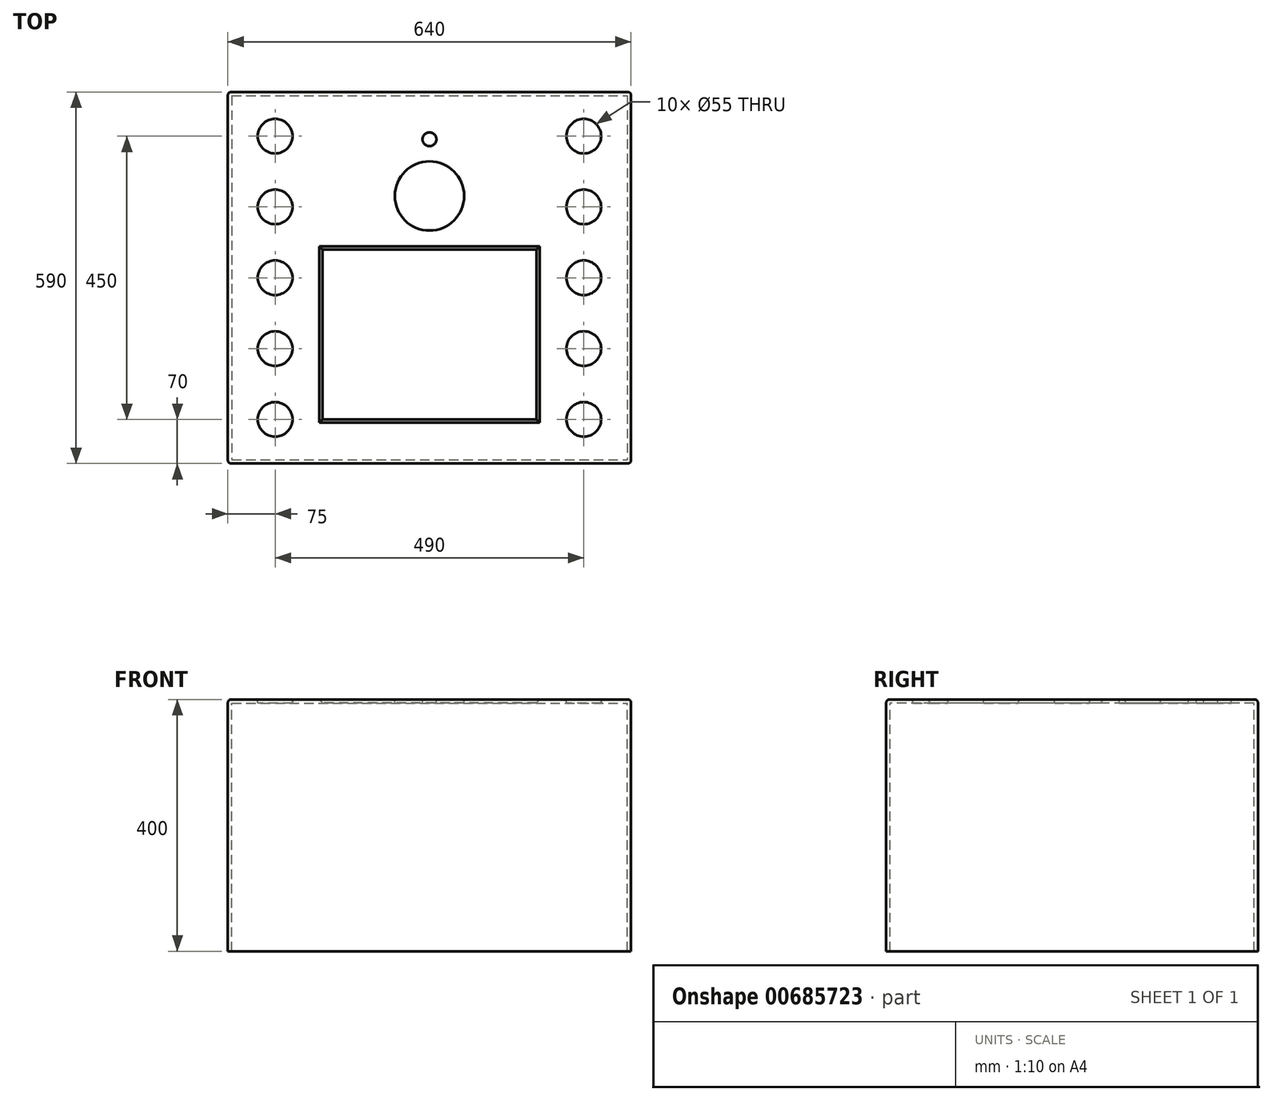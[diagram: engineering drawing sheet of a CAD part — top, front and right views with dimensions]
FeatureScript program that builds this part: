
annotation { "Feature Type Name" : "Feature", "Feature Type Description" : "" }
export const myFeature = defineFeature(function(context is Context, id is Id, definition is map)
    precondition{}
    {
        {
            var Q0;
            Q0=qCreatedBy(makeId("Top.planeOp"),FACE);
            var sketch = newSketch(context, id + "F0", { "sketchPlane" : qUnion([Q0])});
            skLineSegment(sketch, "E0.bottom", {"start": v(320, 295) * mm, "end": v(-320, 295) * mm});
            skLineSegment(sketch, "E0.top", {"start": v(320, -295) * mm, "end": v(-320, -295) * mm});
            skLineSegment(sketch, "E0.left", {"start": v(320, 295) * mm, "end": v(320, -295) * mm});
            skLineSegment(sketch, "E0.right", {"start": v(-320, 295) * mm, "end": v(-320, -295) * mm});
            skPoint(sketch, "E0.middle", {"position": v(0, 0) * mm});
            skLineSegment(sketch, "E1.bottom", {"start": v(170, 45) * mm, "end": v(-170, 45) * mm});
            skLineSegment(sketch, "E1.top", {"start": v(170, -225) * mm, "end": v(-170, -225) * mm});
            skLineSegment(sketch, "E1.left", {"start": v(170, 45) * mm, "end": v(170, -225) * mm});
            skLineSegment(sketch, "E1.right", {"start": v(-170, 45) * mm, "end": v(-170, -225) * mm});
            skPoint(sketch, "E1.middle", {"position": v(0, -90) * mm});
            skCircle(sketch, "E2", {"center": v(0, 130) * mm, "radius": 55 * mm});
            skCircle(sketch, "E3", {"center": v(0, 220) * mm, "radius": 11 * mm});
            skCircle(sketch, "E4", {"center": v(-245, -225) * mm, "radius": 27.5 * mm});
            skCircle(sketch, "E5.0.1.0", {"center": v(-245, -112.5) * mm, "radius": 27.5 * mm});
            skCircle(sketch, "E5.0.2.0", {"center": v(-245, 0) * mm, "radius": 27.5 * mm});
            skCircle(sketch, "E5.0.3.0", {"center": v(-245, 112.5) * mm, "radius": 27.5 * mm});
            skCircle(sketch, "E5.1.0.0", {"center": v(245, -225) * mm, "radius": 27.5 * mm});
            skCircle(sketch, "E5.1.1.0", {"center": v(245, -112.5) * mm, "radius": 27.5 * mm});
            skCircle(sketch, "E5.1.2.0", {"center": v(245, 0) * mm, "radius": 27.5 * mm});
            skCircle(sketch, "E5.1.3.0", {"center": v(245, 112.5) * mm, "radius": 27.5 * mm});
            skLineSegment(sketch, "E5.direction1", {"start": v(-245, -225) * mm, "end": v(245, -225) * mm, "construction": true});
            skLineSegment(sketch, "E5.direction2", {"start": v(-245, -225) * mm, "end": v(-245, -112.5) * mm, "construction": true});
            skLineSegment(sketch, "E6.bottom", {"start": v(-314, 289) * mm, "end": v(314, 289) * mm});
            skLineSegment(sketch, "E6.top", {"start": v(-314, -289) * mm, "end": v(314, -289) * mm});
            skLineSegment(sketch, "E6.left", {"start": v(-314, 289) * mm, "end": v(-314, -289) * mm});
            skLineSegment(sketch, "E6.right", {"start": v(314, 289) * mm, "end": v(314, -289) * mm});
            skCircle(sketch, "E7.0.0.4", {"center": v(-245, 225) * mm, "radius": 27.5 * mm});
            skCircle(sketch, "E7.0.1.4", {"center": v(245, 225) * mm, "radius": 27.5 * mm});
            skSolve(sketch);
        }
        {
            var Q0;
            Q0=makeQuery(id+"F0.imprint","IMPRINT",FACE,{"disambiguationData":[TD([[makeQuery(id+"F0.imprint","IMPRINT",EDGE,{"derivedFrom":sQuery(id+"F0.wireOp",EDGE,"E0.bottom")}),1.0]])]});
            extrude(context, id + "F1", {"entities" : qUnion([Q0]), "oppositeDirection" : true, "depth" : 400 * mm, "offsetDistance" : 25 * mm});
        }
        {
            var Q0;
            Q0=makeQuery(id+"F0.imprint","IMPRINT",FACE,{"disambiguationData":[TD([[makeQuery(id+"F0.imprint","IMPRINT",EDGE,{"derivedFrom":sQuery(id+"F0.wireOp",EDGE,"E1.bottom")}),-1.0]])]});
            extrude(context, id + "F2", {"entities" : qUnion([Q0]), "operationType" : NewBodyOperationType.ADD, "oppositeDirection" : true, "depth" : 6 * mm, "offsetDistance" : 25 * mm});
        }
        {
            var Q0;
            Q0=makeQuery(id+"F1.opExtrude","CAP_EDGE",EDGE,{"disambiguationData":[OSD([sQuery(id+"F0.wireOp",EDGE,"E0.bottom")])],"isStart":true});
            var Q1;
            Q1=makeQuery(id+"F1.opExtrude","CAP_EDGE",EDGE,{"disambiguationData":[OSD([sQuery(id+"F0.wireOp",EDGE,"E0.left")])],"isStart":true});
            var Q2;
            Q2=makeQuery(id+"F1.opExtrude","SWEPT_EDGE",EDGE,{"disambiguationData":[OSD([sQuery(id+"F0.wireOp",EDGE,"E0.bottom"),sQuery(id+"F0.wireOp",EDGE,"E0.left")])]});
            var Q3;
            Q3=makeQuery(id+"F1.opExtrude","SWEPT_EDGE",EDGE,{"disambiguationData":[OSD([sQuery(id+"F0.wireOp",EDGE,"E0.bottom"),sQuery(id+"F0.wireOp",EDGE,"E0.right")])]});
            var Q4;
            Q4=makeQuery(id+"F1.opExtrude","CAP_EDGE",EDGE,{"disambiguationData":[OSD([sQuery(id+"F0.wireOp",EDGE,"E0.right")])],"isStart":true});
            var Q5;
            Q5=makeQuery(id+"F1.opExtrude","SWEPT_EDGE",EDGE,{"disambiguationData":[OSD([sQuery(id+"F0.wireOp",EDGE,"E0.top"),sQuery(id+"F0.wireOp",EDGE,"E0.right")])]});
            var Q6;
            Q6=makeQuery(id+"F1.opExtrude","CAP_EDGE",EDGE,{"disambiguationData":[OSD([sQuery(id+"F0.wireOp",EDGE,"E0.top")])],"isStart":true});
            var Q7;
            Q7=makeQuery(id+"F1.opExtrude","SWEPT_EDGE",EDGE,{"disambiguationData":[OSD([sQuery(id+"F0.wireOp",EDGE,"E0.top"),sQuery(id+"F0.wireOp",EDGE,"E0.left")])]});
            var Q8;
            Q8=makeQuery(id+"F2.opExtrude","CAP_EDGE",EDGE,{"disambiguationData":[OSD([sQuery(id+"F0.wireOp",EDGE,"E5.0.3.0")])],"isStart":true});
            var Q9;
            Q9=makeQuery(id+"F2.opExtrude","CAP_EDGE",EDGE,{"disambiguationData":[OSD([sQuery(id+"F0.wireOp",EDGE,"E5.0.4.0")])],"isStart":true});
            var Q10;
            Q10=makeQuery(id+"F2.opExtrude","CAP_EDGE",EDGE,{"disambiguationData":[OSD([sQuery(id+"F0.wireOp",EDGE,"E5.0.2.0")])],"isStart":true});
            var Q11;
            Q11=makeQuery(id+"F2.opExtrude","CAP_EDGE",EDGE,{"disambiguationData":[OSD([sQuery(id+"F0.wireOp",EDGE,"E5.0.1.0")])],"isStart":true});
            var Q12;
            Q12=makeQuery(id+"F2.opExtrude","CAP_EDGE",EDGE,{"disambiguationData":[OSD([sQuery(id+"F0.wireOp",EDGE,"E5.1.0.0")])],"isStart":true});
            var Q13;
            Q13=makeQuery(id+"F2.opExtrude","CAP_EDGE",EDGE,{"disambiguationData":[OSD([sQuery(id+"F0.wireOp",EDGE,"E5.1.1.0")])],"isStart":true});
            var Q14;
            Q14=makeQuery(id+"F2.opExtrude","CAP_EDGE",EDGE,{"disambiguationData":[OSD([sQuery(id+"F0.wireOp",EDGE,"E4")])],"isStart":true});
            var Q15;
            Q15=makeQuery(id+"F2.opExtrude","CAP_EDGE",EDGE,{"disambiguationData":[OSD([sQuery(id+"F0.wireOp",EDGE,"E5.1.2.0")])],"isStart":true});
            var Q16;
            Q16=makeQuery(id+"F2.opExtrude","CAP_EDGE",EDGE,{"disambiguationData":[OSD([sQuery(id+"F0.wireOp",EDGE,"E5.1.3.0")])],"isStart":true});
            var Q17;
            Q17=makeQuery(id+"F2.opExtrude","CAP_EDGE",EDGE,{"disambiguationData":[OSD([sQuery(id+"F0.wireOp",EDGE,"E5.1.4.0")])],"isStart":true});
            fillet(context, id + "F3", {"entities" : qUnion([Q0, Q1, Q2, Q3, Q4, Q5, Q6, Q7, Q8, Q9, Q10, Q11, Q12, Q13, Q14, Q15, Q16, Q17]), "radius" : 5 * mm, "tangentPropagation" : true, "allowEdgeOverflow" : false});
        }
        {
            var Q0;
            Q0=makeQuery(id+"F2.opExtrude","CAP_EDGE",EDGE,{"disambiguationData":[OSD([sQuery(id+"F0.wireOp",EDGE,"E1.right")])],"isStart":true});
            var Q1;
            Q1=makeQuery(id+"F2.opExtrude","CAP_EDGE",EDGE,{"disambiguationData":[OSD([sQuery(id+"F0.wireOp",EDGE,"E1.bottom")])],"isStart":true});
            var Q2;
            Q2=makeQuery(id+"F2.opExtrude","CAP_EDGE",EDGE,{"disambiguationData":[OSD([sQuery(id+"F0.wireOp",EDGE,"E1.left")])],"isStart":true});
            var Q3;
            Q3=makeQuery(id+"F2.opExtrude","CAP_EDGE",EDGE,{"disambiguationData":[OSD([sQuery(id+"F0.wireOp",EDGE,"E1.top")])],"isStart":true});
            chamfer(context, id + "F4", {"entities" : qUnion([Q0, Q1, Q2, Q3]), "width" : 5 * mm, "tangentPropagation" : true});
        }
    });
